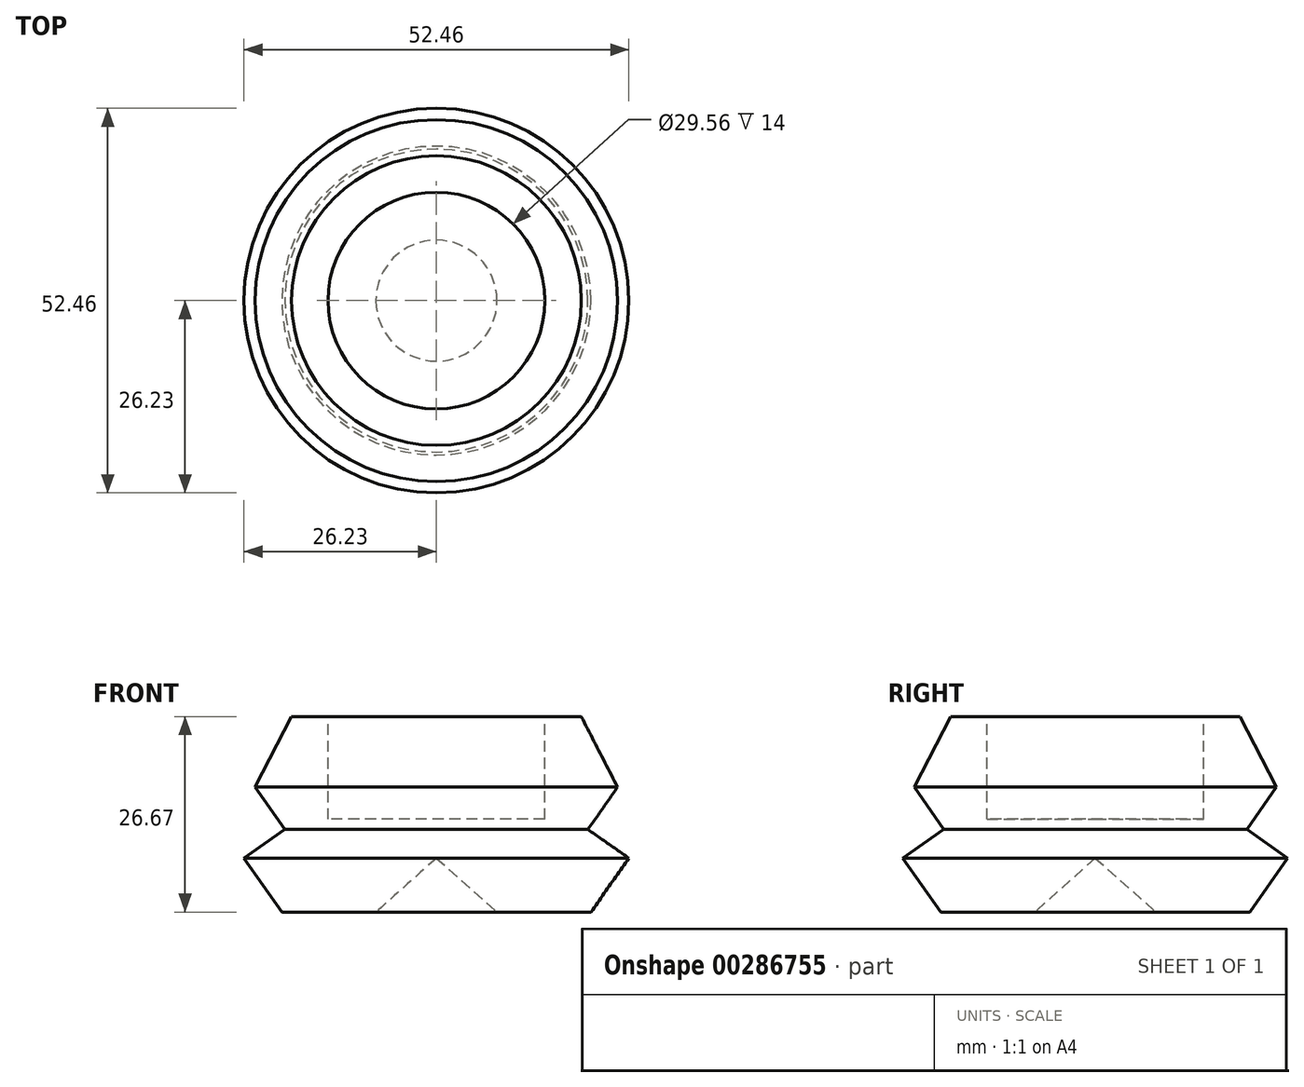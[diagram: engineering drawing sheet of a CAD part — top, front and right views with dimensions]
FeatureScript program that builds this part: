
annotation { "Feature Type Name" : "Feature", "Feature Type Description" : "" }
export const myFeature = defineFeature(function(context is Context, id is Id, definition is map)
    precondition{}
    {
        {
            var Q0;
            Q0=qCreatedBy(makeId("Front.planeOp"),FACE);
            var sketch = newSketch(context, id + "F0", { "sketchPlane" : qUnion([Q0])});
            skLineSegment(sketch, "E0", {"start": v(0, 7.37) * mm, "end": v(-8.25, 0) * mm});
            skLineSegment(sketch, "E1", {"start": v(-8.25, 0) * mm, "end": v(-21.07, 0) * mm});
            skLineSegment(sketch, "E2", {"start": v(-21.07, 0) * mm, "end": v(-26.23, 7.37) * mm});
            skLineSegment(sketch, "E3", {"start": v(-26.23, 7.37) * mm, "end": v(-20.65, 11.27) * mm});
            skLineSegment(sketch, "E4", {"start": v(-20.65, 11.27) * mm, "end": v(-24.7, 17.05) * mm});
            skLineSegment(sketch, "E5", {"start": v(-24.7, 17.05) * mm, "end": v(-19.74, 26.67) * mm});
            skLineSegment(sketch, "E6", {"start": v(-19.74, 26.67) * mm, "end": v(0, 26.67) * mm});
            skLineSegment(sketch, "E7", {"start": v(0, 26.67) * mm, "end": v(0, 7.37) * mm});
            skSolve(sketch);
        }
        {
            var Q0;
            Q0=makeQuery(id+"F0.imprint","IMPRINT",FACE,{"disambiguationData":[TD([[makeQuery(id+"F0.imprint","IMPRINT",EDGE,{"derivedFrom":sQuery(id+"F0.wireOp",EDGE,"E0")}),-1.0]])]});
            var Q1;
            Q1=sQuery(id+"F0.wireOp",EDGE,"E7");
            revolve(context, id + "F1", {"entities" : qUnion([Q0]), "axis" : qUnion([Q1]), "revolveType" : RevolveType.FULL});
        }
        {
            var Q0;
            Q0=makeQuery(id+"F1.opRevolve","SWEPT_FACE",FACE,{"disambiguationData":[OSD([sQuery(id+"F0.wireOp",EDGE,"E6")])]});
            var sketch = newSketch(context, id + "F2", { "sketchPlane" : qUnion([Q0])});
            skSolve(sketch);
        }
        {
            var Q0;
            Q0=makeQuery(id+"F2.imprint","IMPRINT",FACE,{"disambiguationData":[TD([[makeQuery(id+"F2.imprint","IMPRINT",EDGE,{"derivedFrom":makeQuery(id+"F1.opRevolve","SWEPT_EDGE",EDGE,{"disambiguationData":[OSD([sQuery(id+"F0.wireOp",EDGE,"E5"),sQuery(id+"F0.wireOp",EDGE,"E6")])]})}),1.0]])]});
            var sketch = newSketch(context, id + "F3", { "sketchPlane" : qUnion([Q0])});
            skCircle(sketch, "E8", {"center": v(0, 0) * mm, "radius": 14.78 * mm});
            skSolve(sketch);
        }
        {
            var Q0;
            Q0=makeQuery(id+"F3.imprint","IMPRINT",FACE,{"disambiguationData":[TD([[makeQuery(id+"F3.imprint","IMPRINT",EDGE,{"derivedFrom":sQuery(id+"F3.wireOp",EDGE,"E8")}),1.0]])]});
            extrude(context, id + "F4", {"entities" : qUnion([Q0]), "operationType" : NewBodyOperationType.REMOVE, "oppositeDirection" : true, "depth" : 14 * mm});
        }
    });
